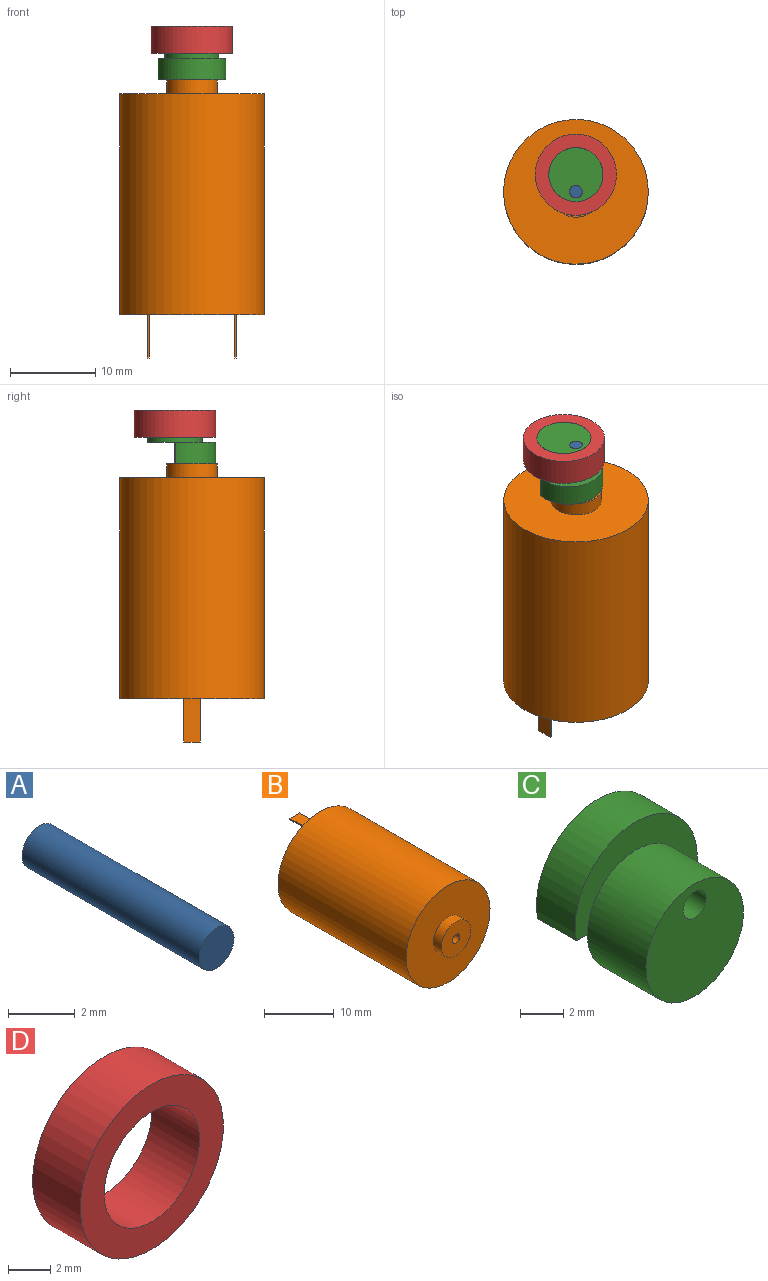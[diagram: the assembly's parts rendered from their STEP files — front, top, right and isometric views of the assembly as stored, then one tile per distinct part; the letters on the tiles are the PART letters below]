
ASSEMBLY  parts=4 mates=5
PART A: 3 faces, bbox 1.5x7.5x1.5 mm
  f0: cylinder r=0.74mm len=7.49mm, axis (0,1,0), area 34.7mm2, adj f1,f2
  f1: plane 1.47x1.47mm, normal (0,-1,0), area 1.7mm2, adj f0
  f2: plane 1.47x1.47mm, normal (0,1,0), area 1.7mm2, adj f0
PART B: 16 faces, bbox 17x32.6x17 mm
  f0: cylinder r=0.74mm len=27.53mm, axis (0,-1,0), area 127.4mm2, adj f2,f5
  f1: cylinder r=8.48mm len=25.91mm, axis (0,-1,0), area 1381mm2, adj f2,f3
  f2: plane 16.97x16.97mm, normal (0,1,0), area 223.6mm2, adj f0,f1,f6,f7,f8,f9,f11,f12
  f3: plane 16.97x16.97mm, normal (0,-1,0), area 198.1mm2, adj f1,f4
  f4: cylinder r=2.98mm len=5.97mm, axis (0,1,0), area 30.5mm2, adj f3,f5
  f5: plane 5.97x5.97mm, normal (0,-1,0), area 26.3mm2, adj f0,f4
  f6: plane 5.08x1.96mm, normal (0,0,1), area 9.9mm2, adj f2,f7,f9,f10
  f7: plane 5.08x0.22mm, normal (1,0,0), area 1.1mm2, adj f2,f6,f8,f10
  f8: plane 5.08x1.96mm, normal (0,0,-1), area 9.9mm2, adj f2,f7,f9,f10
  f9: plane 5.08x0.22mm, normal (-1,0,0), area 1.1mm2, adj f2,f6,f8,f10
  f10: plane 1.96x0.22mm, normal (0,1,0), area 0.4mm2, adj f6,f7,f8,f9
  f11: plane 5.08x1.96mm, normal (0,0,-1), area 9.9mm2, adj f2,f12,f14,f15
  f12: plane 5.08x0.22mm, normal (-1,0,0), area 1.1mm2, adj f2,f11,f13,f15
  f13: plane 5.08x1.96mm, normal (0,0,1), area 9.9mm2, adj f2,f12,f14,f15
  f14: plane 5.08x0.22mm, normal (1,0,0), area 1.1mm2, adj f2,f11,f13,f15
  f15: plane 1.96x0.22mm, normal (0,1,0), area 0.4mm2, adj f11,f12,f13,f14
PART C: 8 faces, bbox 8x6.3x8 mm
  f0: plane 7.95x4.78mm, normal (0,1,0), area 29.4mm2, adj f1,f4,f6
  f1: cylinder r=3.98mm len=7.95mm, axis (0,1,0), area 35.5mm2, adj f0,f5,f6
  f2: plane 6.35x6.35mm, normal (0,-1,0), area 30mm2, adj f3,f4
  f3: cylinder r=3.17mm len=6.35mm, axis (0,1,0), area 76mm2, adj f2,f5,f7
  f4: cylinder r=0.74mm len=6.32mm, axis (0,1,0), area 29.3mm2, adj f0,f2
  f5: plane 7.95x4.78mm, normal (0,-1,0), area 15.3mm2, adj f1,f3,f6
  f6: plane 7.79x2.51mm, normal (0,0,-1), area 19.6mm2, adj f0,f1,f5,f7
  f7: plane 6.35x3.18mm, normal (0,1,0), area 15.8mm2, adj f3,f6
PART D: 4 faces, bbox 9.5x3.2x9.5 mm
  f0: cylinder r=3.17mm len=6.35mm, axis (0,-1,0), area 63.3mm2, adj f2,f3
  f1: cylinder r=4.76mm len=9.53mm, axis (0,-1,0), area 95mm2, adj f2,f3
  f2: plane 9.53x9.53mm, normal (0,1,0), area 39.6mm2, adj f0,f1
  f3: plane 9.53x9.53mm, normal (0,-1,0), area 39.6mm2, adj f0,f1
PLACE A rot(axis=(0,-0.71,-0.71),179.9deg) t=(0,0,6.32)mm
PLACE B rot(axis=(-0.58,-0.58,0.58),120deg) t=(0,0,-1.63)mm
PLACE C rot(axis=(0,0.71,-0.71),179.9deg) t=(0,0,-1.63)mm
PLACE D rot(axis=(-1,0,0),90deg) t=(-0.01,4,-1.24)mm
MATE cylindrical D.f0 <-> C.f3  axis (0,0,1) through (-0.01,2,3.15)mm
MATE planar D.f0 <-> C.f2  axis (0,0,1) through (-0.01,2,6.32)mm
MATE cylindrical A.f0 <-> B.f4  axis (0,0,-1) through (0,0,-1.17)mm
MATE planar C.f0 <-> B.f0  axis (0,0,-1) through (0,-0.07,0)mm
MATE fastened A.f0 <-> C.f4  axis (0,0,1) through (0,0,6.32)mm
